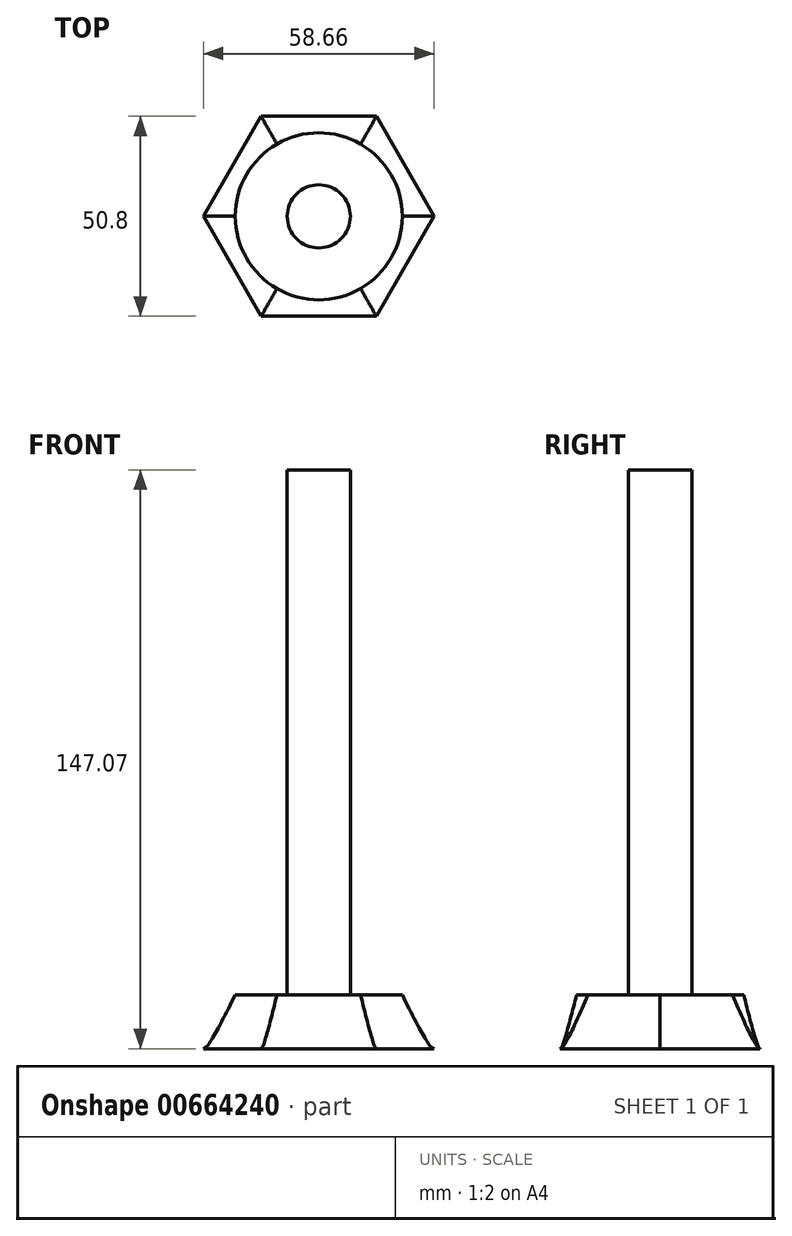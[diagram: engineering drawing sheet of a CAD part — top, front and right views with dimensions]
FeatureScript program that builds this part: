
annotation { "Feature Type Name" : "Feature", "Feature Type Description" : "" }
export const myFeature = defineFeature(function(context is Context, id is Id, definition is map)
    precondition{}
    {
        {
            var Q0;
            Q0=qCreatedBy(makeId("Top.planeOp"),FACE);
            cPlane(context, id + "F0", {"entities" : qUnion([Q0]), "cplaneType" : CPlaneType.OFFSET, "offset" : 13.72 * mm, "width" : 152.4 * mm, "height" : 152.4 * mm});
        }
        {
            var Q0;
            Q0=qCreatedBy(makeId("Top.planeOp"),FACE);
            var sketch = newSketch(context, id + "F1", { "sketchPlane" : qUnion([Q0])});
            skCircle(sketch, "E0.cCircle", {"center": v(0, 0) * mm, "radius": 25.4 * mm, "construction": true});
            skLineSegment(sketch, "E0.0", {"start": v(14.66, -25.4) * mm, "end": v(-14.66, -25.4) * mm});
            skLineSegment(sketch, "E0.1", {"start": v(-14.66, -25.4) * mm, "end": v(-29.33, 0) * mm});
            skLineSegment(sketch, "E0.2", {"start": v(-29.33, 0) * mm, "end": v(-14.66, 25.4) * mm});
            skLineSegment(sketch, "E0.3", {"start": v(-14.66, 25.4) * mm, "end": v(14.66, 25.4) * mm});
            skLineSegment(sketch, "E0.4", {"start": v(14.66, 25.4) * mm, "end": v(29.33, 0) * mm});
            skLineSegment(sketch, "E0.5", {"start": v(29.33, 0) * mm, "end": v(14.66, -25.4) * mm});
            skPoint(sketch, "E0.0.midPoint", {"position": v(0, -25.4) * mm});
            skSolve(sketch);
        }
        {
            var Q0;
            Q0=qCreatedBy(id+"F0.planeOp",FACE);
            var sketch = newSketch(context, id + "F2", { "sketchPlane" : qUnion([Q0])});
            skCircle(sketch, "E1", {"center": v(0, 0) * mm, "radius": 21.22 * mm});
            skSolve(sketch);
        }
        {
            var Q0;
            Q0 = qSketchRegion(id + "F1", true);
            var Q1;
            Q1 = qSketchRegion(id + "F2", true);
            loft(context, id + "F3", {"startCondition" : LoftEndDerivativeType.TANGENT_TO_PROFILE, "startMagnitude" : 0.5, "sheetProfilesArray" : [{ "sheetProfileEntities" : qUnion([Q0]) }, { "sheetProfileEntities" : qUnion([Q1]) }]});
        }
        {
            var Q0;
            Q0=makeQuery(id+"F3.opLoft","CAP_FACE",FACE,{"disambiguationData":[OSD([makeQuery(id+"F2.imprint","IMPRINT",FACE,{"disambiguationData":[TD([[makeQuery(id+"F2.imprint","IMPRINT",EDGE,{"derivedFrom":sQuery(id+"F2.wireOp",EDGE,"E1")}),1.0]])]})])],"isStart":true});
            var sketch = newSketch(context, id + "F4", { "sketchPlane" : qUnion([Q0])});
            skCircle(sketch, "E2", {"center": v(0, 0) * mm, "radius": 8.02 * mm});
            skSolve(sketch);
        }
        {
            var Q0;
            Q0 = qSketchRegion(id + "F4", true);
            extrude(context, id + "F5", {"entities" : qUnion([Q0]), "operationType" : NewBodyOperationType.ADD, "depth" : 133.35 * mm, "offsetDistance" : 25.4 * mm});
        }
    });
